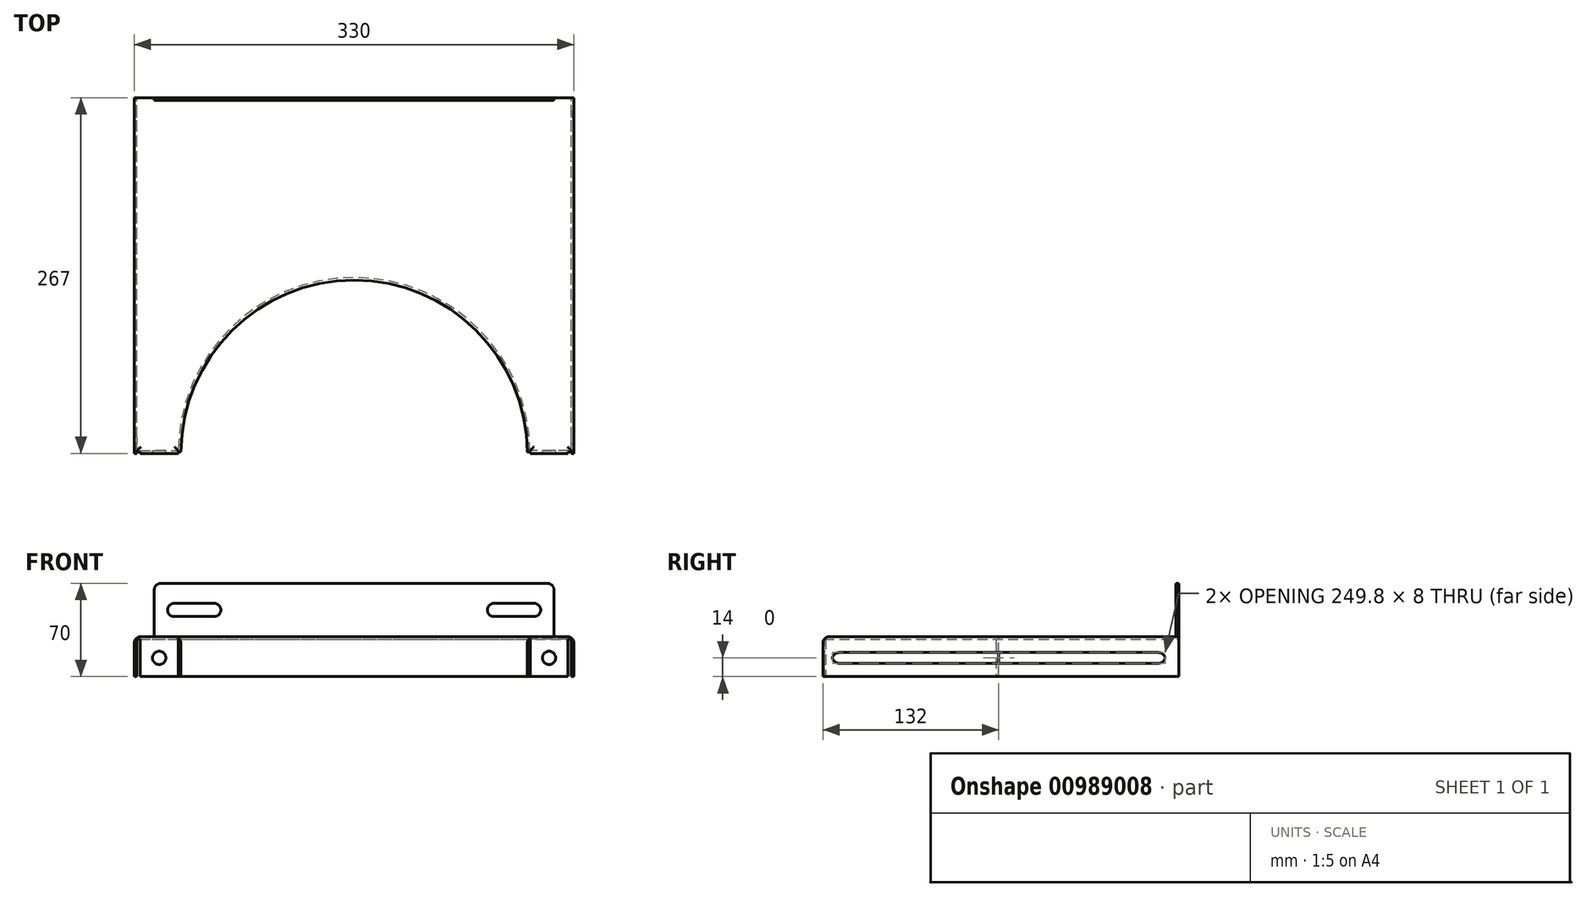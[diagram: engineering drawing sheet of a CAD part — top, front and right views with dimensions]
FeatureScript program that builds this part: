
annotation { "Feature Type Name" : "Feature", "Feature Type Description" : "" }
export const myFeature = defineFeature(function(context is Context, id is Id, definition is map)
    precondition{}
    {
        {
            var Q0;
            Q0=qCreatedBy(makeId("Front.planeOp"),FACE);
            var sketch = newSketch(context, id + "F0", { "sketchPlane" : qUnion([Q0])});
            skLineSegment(sketch, "E0", {"start": v(-163, -30) * mm, "end": v(-163, -2) * mm});
            skLineSegment(sketch, "E1", {"start": v(-163, -2) * mm, "end": v(0, -2) * mm});
            skLineSegment(sketch, "E2", {"start": v(0, 0) * mm, "end": v(-165, 0) * mm});
            skLineSegment(sketch, "E3", {"start": v(-165, 0) * mm, "end": v(-165, -30) * mm});
            skLineSegment(sketch, "E4", {"start": v(-163, -30) * mm, "end": v(-165, -30) * mm});
            skLineSegment(sketch, "E5", {"start": v(0, 0) * mm, "end": v(0, -2) * mm});
            skSolve(sketch);
        }
        {
            var Q0;
            Q0=qSketchRegion(id+"F0",true);
            extrude(context, id + "F1", {"entities" : qUnion([Q0]), "depth" : 267 * mm, "offsetDistance" : 25 * mm});
        }
        {
            var Q0;
            Q0=makeQuery(id+"F1.opExtrude","SWEPT_FACE",FACE,{"disambiguationData":[OSD([sQuery(id+"F0.wireOp",EDGE,"E3")])]});
            var sketch = newSketch(context, id + "F2", { "sketchPlane" : qUnion([Q0])});
            skLineSegment(sketch, "E6.bottom", {"start": v(10, -12) * mm, "end": v(260, -12) * mm});
            skLineSegment(sketch, "E6.top", {"start": v(10, -20) * mm, "end": v(260, -20) * mm});
            skLineSegment(sketch, "E6.left", {"start": v(10, -12) * mm, "end": v(10, -20) * mm});
            skLineSegment(sketch, "E6.right", {"start": v(260, -12) * mm, "end": v(260, -20) * mm});
            skLineSegment(sketch, "E7", {"start": v(10, -20) * mm, "end": v(0, -20) * mm});
            skLineSegment(sketch, "E8", {"start": v(0, -20) * mm, "end": v(10, -20) * mm, "construction": true});
            skLineSegment(sketch, "E9", {"start": v(10, -20) * mm, "end": v(10, -30) * mm, "construction": true});
            skSolve(sketch);
        }
        {
            var Q0;
            Q0=qSketchRegion(id+"F2",true);
            extrude(context, id + "F3", {"entities" : qUnion([Q0]), "endBound" : BoundingType.SYMMETRIC, "depth" : 10 * mm, "offsetDistance" : 25 * mm});
        }
        {
            var Q0;
            Q0=makeQuery(id+"F1.opExtrude","SWEPT_FACE",FACE,{"disambiguationData":[OSD([sQuery(id+"F0.wireOp",EDGE,"E2")])]});
            var sketch = newSketch(context, id + "F4", { "sketchPlane" : qUnion([Q0])});
            skCircle(sketch, "E10", {"center": v(0, -267) * mm, "radius": 130 * mm});
            skSolve(sketch);
        }
        {
            var Q0;
            Q0=qSketchRegion(id+"F4",true);
            extrude(context, id + "F5", {"entities" : qUnion([Q0]), "endBound" : BoundingType.SYMMETRIC, "depth" : 25 * mm, "offsetDistance" : 25 * mm});
        }
        {
            var Q0;
            Q0=makeQuery(id+"F1.opExtrude","CAP_FACE",FACE,{"disambiguationData":[OSD([sQuery(id+"F0.wireOp",EDGE,"E0"),sQuery(id+"F0.wireOp",EDGE,"E1"),sQuery(id+"F0.wireOp",EDGE,"E2"),sQuery(id+"F0.wireOp",EDGE,"E3"),sQuery(id+"F0.wireOp",EDGE,"E4"),sQuery(id+"F0.wireOp",EDGE,"E5")])],"isStart":true});
            var sketch = newSketch(context, id + "F6", { "sketchPlane" : qUnion([Q0])});
            skLineSegment(sketch, "E11", {"start": v(150, 0) * mm, "end": v(150, 40) * mm});
            skLineSegment(sketch, "E12", {"start": v(150, 40) * mm, "end": v(0, 40) * mm});
            skLineSegment(sketch, "E13", {"start": v(0, 40) * mm, "end": v(0, 0) * mm});
            skSolve(sketch);
        }
        {
            var Q0;
            {var subQ0=sQuery(id+"F6.wireOp",EDGE,"E11");Q0=makeQuery(id+"F6.imprint","IMPRINT",FACE,{"disambiguationData":[TD([[makeQuery(id+"F6.imprint","IMPRINT",EDGE,{"derivedFrom":subQ0}),1.0]])]});}
            extrude(context, id + "F7", {"entities" : qUnion([Q0]), "oppositeDirection" : true, "depth" : 2 * mm, "offsetDistance" : 25 * mm});
        }
        {
            var Q0;
            Q0=makeQuery(id+"F7.opExtrude","CAP_FACE",FACE,{"disambiguationData":[OSD([sQuery(id+"F0.wireOp",EDGE,"E2"),sQuery(id+"F6.wireOp",EDGE,"E11"),sQuery(id+"F6.wireOp",EDGE,"E12"),sQuery(id+"F6.wireOp",EDGE,"E13")])],"isStart":false});
            var sketch = newSketch(context, id + "F8", { "sketchPlane" : qUnion([Q0])});
            skLineSegment(sketch, "E14.bottom", {"start": v(-140, 25) * mm, "end": v(-100, 25) * mm});
            skLineSegment(sketch, "E14.top", {"start": v(-140, 15) * mm, "end": v(-100, 15) * mm});
            skLineSegment(sketch, "E14.left", {"start": v(-140, 25) * mm, "end": v(-140, 15) * mm});
            skLineSegment(sketch, "E14.right", {"start": v(-100, 25) * mm, "end": v(-100, 15) * mm});
            skLineSegment(sketch, "E15", {"start": v(-140, 15) * mm, "end": v(-150, 15) * mm});
            skLineSegment(sketch, "E16", {"start": v(-150, 15) * mm, "end": v(-140, 15) * mm, "construction": true});
            skLineSegment(sketch, "E17", {"start": v(-140, 0) * mm, "end": v(-140, 15) * mm, "construction": true});
            skSolve(sketch);
        }
        {
            var Q0;
            Q0=qSketchRegion(id+"F8",true);
            extrude(context, id + "F9", {"entities" : qUnion([Q0]), "endBound" : BoundingType.SYMMETRIC, "depth" : 25 * mm, "offsetDistance" : 25 * mm});
        }
        {
            var Q0;
            Q0=makeQuery(id+"F9.opExtrude","SWEPT_EDGE",EDGE,{"disambiguationData":[OSD([sQuery(id+"F8.wireOp",EDGE,"E14.bottom"),sQuery(id+"F8.wireOp",EDGE,"E14.left")])]});
            var Q1;
            Q1=makeQuery(id+"F9.opExtrude","SWEPT_EDGE",EDGE,{"disambiguationData":[OSD([sQuery(id+"F8.wireOp",EDGE,"E14.top"),sQuery(id+"F8.wireOp",EDGE,"E14.left")])]});
            var Q2;
            Q2=makeQuery(id+"F9.opExtrude","SWEPT_EDGE",EDGE,{"disambiguationData":[OSD([sQuery(id+"F8.wireOp",EDGE,"E14.top"),sQuery(id+"F8.wireOp",EDGE,"E14.right")])]});
            var Q3;
            Q3=makeQuery(id+"F9.opExtrude","SWEPT_EDGE",EDGE,{"disambiguationData":[OSD([sQuery(id+"F8.wireOp",EDGE,"E14.bottom"),sQuery(id+"F8.wireOp",EDGE,"E14.right")])]});
            var Q4;
            Q4=makeQuery(id+"F3.opExtrude","SWEPT_EDGE",EDGE,{"disambiguationData":[OSD([sQuery(id+"F2.wireOp",EDGE,"E6.bottom"),sQuery(id+"F2.wireOp",EDGE,"E6.left")])]});
            var Q5;
            Q5=makeQuery(id+"F3.opExtrude","SWEPT_EDGE",EDGE,{"disambiguationData":[OSD([sQuery(id+"F2.wireOp",EDGE,"E6.top"),sQuery(id+"F2.wireOp",EDGE,"E6.left")])]});
            var Q6;
            Q6=makeQuery(id+"F3.opExtrude","SWEPT_EDGE",EDGE,{"disambiguationData":[OSD([sQuery(id+"F2.wireOp",EDGE,"E6.top"),sQuery(id+"F2.wireOp",EDGE,"E6.right")])]});
            var Q7;
            Q7=makeQuery(id+"F3.opExtrude","SWEPT_EDGE",EDGE,{"disambiguationData":[OSD([sQuery(id+"F2.wireOp",EDGE,"E6.bottom"),sQuery(id+"F2.wireOp",EDGE,"E6.right")])]});
            fillet(context, id + "F10", {"entities" : qUnion([Q0, Q1, Q2, Q3, Q4, Q5, Q6, Q7]), "radius" : 5 * mm, "tangentPropagation" : true, "allowEdgeOverflow" : false});
        }
        {
            var Q0;
            Q0=makeQuery(id+"F1.opExtrude","CAP_FACE",FACE,{"disambiguationData":[OSD([sQuery(id+"F0.wireOp",EDGE,"E0"),sQuery(id+"F0.wireOp",EDGE,"E1"),sQuery(id+"F0.wireOp",EDGE,"E2"),sQuery(id+"F0.wireOp",EDGE,"E3"),sQuery(id+"F0.wireOp",EDGE,"E4"),sQuery(id+"F0.wireOp",EDGE,"E5")])],"isStart":false});
            var sketch = newSketch(context, id + "F11", { "sketchPlane" : qUnion([Q0])});
            skLineSegment(sketch, "E18.bottom", {"start": v(-160.5, -2) * mm, "end": v(-132.06, -2) * mm});
            skLineSegment(sketch, "E18.top", {"start": v(-160.5, -30) * mm, "end": v(-132.06, -30) * mm});
            skLineSegment(sketch, "E18.left", {"start": v(-160.5, -2) * mm, "end": v(-160.5, -30) * mm});
            skLineSegment(sketch, "E18.right", {"start": v(-132.06, -2) * mm, "end": v(-132.06, -30) * mm});
            skSolve(sketch);
        }
        {
            var Q0;
            Q0=makeQuery(id+"F11.imprint","IMPRINT",FACE,{"disambiguationData":[TD([[makeQuery(id+"F11.imprint","IMPRINT",EDGE,{"derivedFrom":sQuery(id+"F11.wireOp",EDGE,"E18.bottom")}),-1.0]])]});
            extrude(context, id + "F12", {"entities" : qUnion([Q0]), "oppositeDirection" : true, "depth" : 2 * mm, "offsetDistance" : 25 * mm});
        }
        {
            var Q0;
            Q0=makeQuery(id+"F15.opBoolean","MERGE",FACE,{"derivedFrom":[makeQuery(id+"F1.opExtrude","CAP_FACE",FACE,{"disambiguationData":[OSD([sQuery(id+"F0.wireOp",EDGE,"E0"),sQuery(id+"F0.wireOp",EDGE,"E1"),sQuery(id+"F0.wireOp",EDGE,"E2"),sQuery(id+"F0.wireOp",EDGE,"E3"),sQuery(id+"F0.wireOp",EDGE,"E4"),sQuery(id+"F0.wireOp",EDGE,"E5")])],"isStart":false}),makeQuery(id+"F12.opExtrude","CAP_FACE",FACE,{"disambiguationData":[OSD([sQuery(id+"F11.wireOp",EDGE,"E18.bottom"),sQuery(id+"F11.wireOp",EDGE,"E18.top"),sQuery(id+"F11.wireOp",EDGE,"E18.left"),sQuery(id+"F11.wireOp",EDGE,"E18.right")])],"isStart":true})]});
            var sketch = newSketch(context, id + "F13", { "sketchPlane" : qUnion([Q0])});
            skCircle(sketch, "E19", {"center": v(-146.28, -16) * mm, "radius": 5 * mm});
            skSolve(sketch);
        }
        {
            var Q0;
            Q0=makeQuery(id+"F13.imprint","IMPRINT",FACE,{"disambiguationData":[TD([[makeQuery(id+"F13.imprint","IMPRINT",EDGE,{"derivedFrom":sQuery(id+"F13.wireOp",EDGE,"E19")}),1.0]])]});
            var Q1;
            Q1=sQuery(id+"F13.wireOp",EDGE,"E19");
            extrude(context, id + "F14", {"entities" : qUnion([Q0]), "surfaceEntities" : qUnion([Q1]), "endBound" : BoundingType.SYMMETRIC, "depth" : 10 * mm, "offsetDistance" : 25 * mm});
        }
        {
            var Q0;
            Q0=makeQuery(id+"F1.opExtrude","SWEPT_BODY",BODY,{"disambiguationData":[OSD([sQuery(id+"F0.wireOp",EDGE,"E0"),sQuery(id+"F0.wireOp",EDGE,"E1"),sQuery(id+"F0.wireOp",EDGE,"E2"),sQuery(id+"F0.wireOp",EDGE,"E3"),sQuery(id+"F0.wireOp",EDGE,"E4"),sQuery(id+"F0.wireOp",EDGE,"E5")])]});
            var Q1;
            Q1=makeQuery(id+"F7.opExtrude","SWEPT_BODY",BODY,{"disambiguationData":[OSD([sQuery(id+"F0.wireOp",EDGE,"E2"),sQuery(id+"F6.wireOp",EDGE,"E11"),sQuery(id+"F6.wireOp",EDGE,"E12"),sQuery(id+"F6.wireOp",EDGE,"E13")])]});
            var Q2;
            Q2=makeQuery(id+"F12.opExtrude","SWEPT_BODY",BODY,{"disambiguationData":[OSD([sQuery(id+"F11.wireOp",EDGE,"E18.bottom"),sQuery(id+"F11.wireOp",EDGE,"E18.top"),sQuery(id+"F11.wireOp",EDGE,"E18.left"),sQuery(id+"F11.wireOp",EDGE,"E18.right")])]});
            booleanBodies(context, id + "F15", {"operationType" : BooleanOperationType.UNION, "tools" : qUnion([Q0, Q1, Q2])});
        }
        {
            var Q0;
            Q0=makeQuery(id+"F9.opExtrude","SWEPT_BODY",BODY,{"disambiguationData":[OSD([sQuery(id+"F8.wireOp",EDGE,"E14.bottom"),sQuery(id+"F8.wireOp",EDGE,"E14.top"),sQuery(id+"F8.wireOp",EDGE,"E14.left"),sQuery(id+"F8.wireOp",EDGE,"E14.right")])]});
            var Q1;
            Q1=makeQuery(id+"F3.opExtrude","SWEPT_BODY",BODY,{"disambiguationData":[OSD([sQuery(id+"F2.wireOp",EDGE,"E6.bottom"),sQuery(id+"F2.wireOp",EDGE,"E6.top"),sQuery(id+"F2.wireOp",EDGE,"E6.left"),sQuery(id+"F2.wireOp",EDGE,"E6.right")])]});
            var Q2;
            Q2=makeQuery(id+"F5.opExtrude","SWEPT_BODY",BODY,{"disambiguationData":[OSD([sQuery(id+"F4.wireOp",EDGE,"E10")])]});
            var Q3;
            Q3=makeQuery(id+"F14.opExtrude","SWEPT_BODY",BODY,{"disambiguationData":[OSD([sQuery(id+"F13.wireOp",EDGE,"E19")])]});
            var Q4;
            Q4=makeQuery(id+"F1.opExtrude","SWEPT_BODY",BODY,{"disambiguationData":[OSD([sQuery(id+"F0.wireOp",EDGE,"E0"),sQuery(id+"F0.wireOp",EDGE,"E1"),sQuery(id+"F0.wireOp",EDGE,"E2"),sQuery(id+"F0.wireOp",EDGE,"E3"),sQuery(id+"F0.wireOp",EDGE,"E4"),sQuery(id+"F0.wireOp",EDGE,"E5")])]});
            booleanBodies(context, id + "F16", {"operationType" : BooleanOperationType.SUBTRACTION, "tools" : qUnion([Q0, Q1, Q2, Q3]), "targets" : qUnion([Q4])});
        }
        {
            var Q0;
            Q0=makeQuery(id+"F7.opExtrude","SWEPT_EDGE",EDGE,{"disambiguationData":[OSD([sQuery(id+"F6.wireOp",EDGE,"E11"),sQuery(id+"F6.wireOp",EDGE,"E12")])]});
            var Q1;
            Q1=makeQuery(id+"F1.opExtrude","SWEPT_EDGE",EDGE,{"disambiguationData":[OSD([sQuery(id+"F0.wireOp",EDGE,"E2"),sQuery(id+"F0.wireOp",EDGE,"E3")])]});
            var Q2;
            Q2=makeQuery(id+"F1.opExtrude","CAP_EDGE",EDGE,{"disambiguationData":[OSD([sQuery(id+"F0.wireOp",EDGE,"E2")])],"isStart":false});
            fillet(context, id + "F17", {"entities" : qUnion([Q0, Q1, Q2]), "radius" : 5 * mm, "tangentPropagation" : true, "allowEdgeOverflow" : false});
        }
        {
            var Q0;
            Q0=makeQuery(id+"F1.opExtrude","SWEPT_BODY",BODY,{"disambiguationData":[OSD([sQuery(id+"F0.wireOp",EDGE,"E0"),sQuery(id+"F0.wireOp",EDGE,"E1"),sQuery(id+"F0.wireOp",EDGE,"E2"),sQuery(id+"F0.wireOp",EDGE,"E3"),sQuery(id+"F0.wireOp",EDGE,"E4"),sQuery(id+"F0.wireOp",EDGE,"E5")])]});
            var Q1;
            Q1=makeQuery(id+"F7.opExtrude","SWEPT_BODY",BODY,{"disambiguationData":[OSD([sQuery(id+"F0.wireOp",EDGE,"E2"),sQuery(id+"F6.wireOp",EDGE,"E11"),sQuery(id+"F6.wireOp",EDGE,"E12"),sQuery(id+"F6.wireOp",EDGE,"E13")])]});
            var Q2;
            Q2=qCreatedBy(makeId("Right.planeOp"),FACE);
            mirror(context, id + "F18", {"operationType" : NewBodyOperationType.ADD, "entities" : qUnion([Q0, Q1]), "mirrorPlane" : qUnion([Q2])});
        }
        {
            var Q0;
            {var subQ0=makeQuery(id+"F1.opExtrude","SWEPT_FACE",FACE,{"disambiguationData":[OSD([sQuery(id+"F0.wireOp",EDGE,"E1")])]});Q0=makeQuery(id+"F18.boolean.opBoolean","MERGE",FACE,{"derivedFrom":[subQ0,makeQuery(id+"F18.opPattern","COPY",FACE,{"derivedFrom":subQ0,"instanceName":"1"})]});}
            var sketch = newSketch(context, id + "F19", { "sketchPlane" : qUnion([Q0])});
            skArc(sketch, "E20.0", {"start": v(-130, 266) * mm, "mid": v(0, 137) * mm, "end": v(130, 266) * mm});
            skArc(sketch, "E21", {"start": v(-132, 266) * mm, "mid": v(0, 135) * mm, "end": v(132, 266) * mm});
            skLineSegment(sketch, "E22", {"start": v(130, 266) * mm, "end": v(132.06, 266) * mm});
            skLineSegment(sketch, "E23", {"start": v(-130, 266) * mm, "end": v(-132.06, 266) * mm});
            skSolve(sketch);
        }
        {
            var Q0;
            Q0 = qSketchRegion(id + "F19", true);
            extrude(context, id + "F20", {"entities" : qUnion([Q0]), "operationType" : NewBodyOperationType.ADD, "depth" : 28 * mm, "offsetDistance" : 25 * mm});
        }
        {
            var Q0;
            {var subQ0=makeQuery(id+"F16.opBoolean","INTERSECT",EDGE,{"derivedFrom":[makeQuery(id+"F5.opExtrude","SWEPT_FACE",FACE,{"disambiguationData":[OSD([sQuery(id+"F4.wireOp",EDGE,"E10")])]}),makeQuery(id+"F1.opExtrude","SWEPT_FACE",FACE,{"disambiguationData":[OSD([sQuery(id+"F0.wireOp",EDGE,"E2")])]})]});Q0=makeQuery(id+"F18.boolean.opBoolean","MERGE",EDGE,{"derivedFrom":[subQ0,makeQuery(id+"F18.opPattern","COPY",EDGE,{"derivedFrom":subQ0,"instanceName":"1"})]});}
            fillet(context, id + "F21", {"entities" : qUnion([Q0]), "radius" : 5 * mm, "tangentPropagation" : true, "allowEdgeOverflow" : false});
        }
    });
